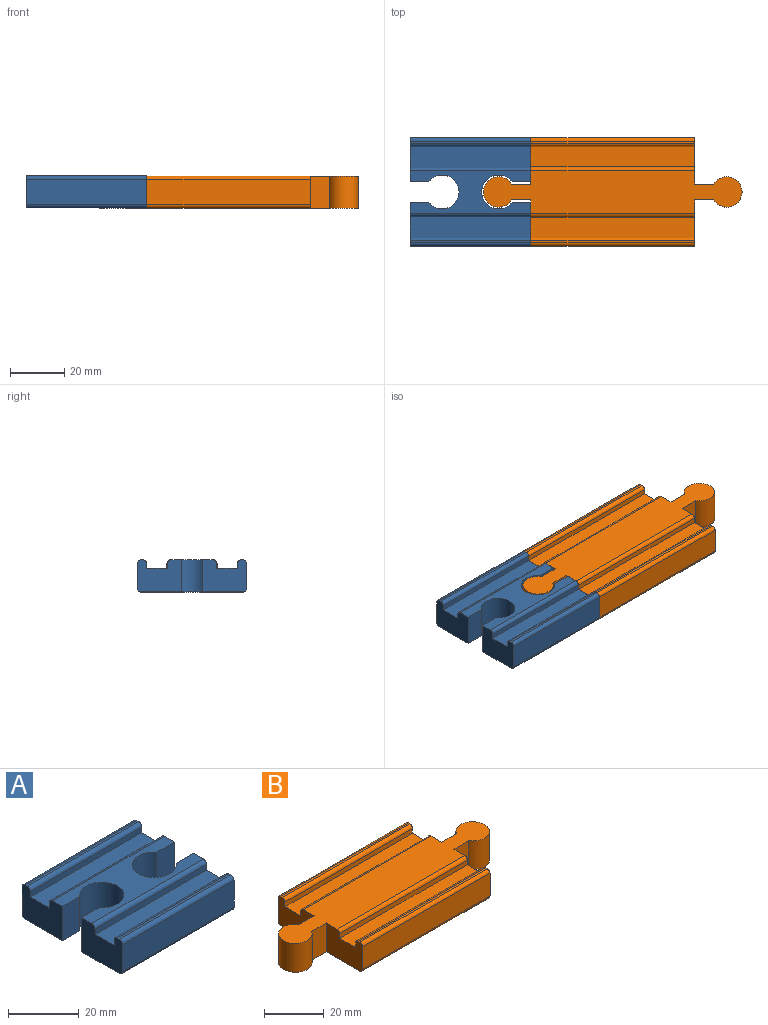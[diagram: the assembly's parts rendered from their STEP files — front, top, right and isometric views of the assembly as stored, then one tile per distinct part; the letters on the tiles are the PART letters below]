
ASSEMBLY  parts=2 mates=1
PART A: 30 faces, bbox 44.5x40x11.8 mm
  f0: plane 16.19x11.81mm, normal (-1,0,0), area 165.7mm2, adj f2,f3,f7,f9,f13,f14,f15,f18
  f1: plane 16.19x11.81mm, normal (1,0,0), area 165.7mm2, adj f2,f3,f7,f9,f13,f14,f15,f18
  f2: plane 44.45x15.62mm, normal (0,0,1), area 359.6mm2, adj f0,f1,f6,f8,f16,f18,f24,f25
  f3: plane 44.45x37.47mm, normal (0,0,-1), area 1330.5mm2, adj f0,f1,f6,f8,f20,f21,f24,f25
  f4: plane 44.45x0.76mm, normal (0,0,1), area 33.9mm2, adj f6,f8,f17,f23
  f5: plane 44.45x9.27mm, normal (0,1,0), area 412.1mm2, adj f6,f8,f21,f23
  f6: plane 16.19x11.81mm, normal (-1,0,0), area 165.7mm2, adj f2,f3,f4,f5,f10,f11,f12,f16
  f7: plane 44.45x9.27mm, normal (0,-1,0), area 412.1mm2, adj f0,f1,f20,f22
  f8: plane 16.19x11.81mm, normal (1,0,0), area 165.7mm2, adj f2,f3,f4,f5,f10,f11,f12,f16
  f9: plane 44.45x0.76mm, normal (0,0,1), area 33.9mm2, adj f0,f1,f19,f22
  f10: plane 44.45x1.91mm, normal (0,1,0), area 84.7mm2, adj f6,f8,f12,f16
  f11: plane 44.45x1.91mm, normal (0,-1,0), area 84.7mm2, adj f6,f8,f12,f17
  f12: plane 44.45x7.62mm, normal (0,0,1), area 338.7mm2, adj f6,f8,f10,f11
  f13: plane 44.45x1.91mm, normal (0,1,0), area 84.7mm2, adj f0,f1,f15,f19
  f14: plane 44.45x1.91mm, normal (0,-1,0), area 84.7mm2, adj f0,f1,f15,f18
  f15: plane 44.45x7.62mm, normal (0,0,1), area 338.7mm2, adj f0,f1,f13,f14
  f16: cylinder r=1.27mm len=44.45mm, axis (-1,0,0), area 88.7mm2, adj f2,f6,f8,f10
  f17: cylinder r=1.27mm len=44.45mm, axis (1,0,0), area 88.7mm2, adj f4,f6,f8,f11
  f18: cylinder r=1.27mm len=44.45mm, axis (1,0,0), area 88.7mm2, adj f0,f1,f2,f14
  f19: cylinder r=1.27mm len=44.45mm, axis (-1,0,0), area 88.7mm2, adj f0,f1,f9,f13
  f20: cylinder r=1.27mm len=44.45mm, axis (1,0,0), area 88.7mm2, adj f0,f1,f3,f7
  f21: cylinder r=1.27mm len=44.45mm, axis (-1,0,0), area 88.7mm2, adj f3,f5,f6,f8
  f22: cylinder r=1.27mm len=44.45mm, axis (-1,0,0), area 88.7mm2, adj f0,f1,f7,f9
  f23: cylinder r=1.27mm len=44.45mm, axis (1,0,0), area 88.7mm2, adj f4,f5,f6,f8
  f24: plane 11.81x6.89mm, normal (0,-1,0), area 81.4mm2, adj f2,f3,f8,f25
  f25: cylinder r=6.22mm len=12.45mm, axis (0,0,1), area 365mm2, adj f2,f3,f24,f26
  f26: plane 11.81x6.89mm, normal (0,1,0), area 81.4mm2, adj f1,f2,f3,f25
  f27: plane 11.81x6.89mm, normal (0,-1,0), area 81.4mm2, adj f2,f3,f6,f29
  f28: plane 11.81x6.89mm, normal (0,1,0), area 81.4mm2, adj f0,f2,f3,f29
  f29: cylinder r=6.22mm len=12.45mm, axis (0,0,1), area 365mm2, adj f2,f3,f27,f28
PART B: 30 faces, bbox 95.1x40x11.8 mm
  f0: plane 95.12x15.88mm, normal (0,0,1), area 1229.7mm2, adj f2,f3,f5,f7,f10,f11,f12,f13
  f1: plane 60.33x0.76mm, normal (0,0,1), area 46mm2, adj f5,f7,f23,f29
  f2: plane 17.08x11.81mm, normal (-1,0,0), area 176.6mm2, adj f0,f6,f8,f9,f15,f19,f20,f21
  f3: plane 17.08x11.81mm, normal (1,0,0), area 176.6mm2, adj f0,f6,f8,f9,f11,f19,f20,f21
  f4: plane 60.33x9.27mm, normal (0,1,0), area 559.3mm2, adj f5,f7,f27,f29
  f5: plane 17.08x11.81mm, normal (-1,0,0), area 176.6mm2, adj f0,f1,f4,f9,f13,f16,f17,f18
  f6: plane 60.33x9.27mm, normal (0,-1,0), area 559.3mm2, adj f2,f3,f26,f28
  f7: plane 17.08x11.81mm, normal (1,0,0), area 176.6mm2, adj f0,f1,f4,f9,f10,f16,f17,f18
  f8: plane 60.33x0.76mm, normal (0,0,1), area 46mm2, adj f2,f3,f24,f28
  f9: plane 95.12x37.47mm, normal (0,0,-1), area 2532.1mm2, adj f2,f3,f5,f7,f10,f11,f12,f13
  f10: plane 11.81x7.05mm, normal (0,1,0), area 83.2mm2, adj f0,f7,f9,f12
  f11: plane 11.81x7.05mm, normal (0,-1,0), area 83.2mm2, adj f0,f3,f9,f12
  f12: cylinder r=5.59mm len=11.81mm, axis (0,0,1), area 342.1mm2, adj f0,f9,f10,f11
  f13: plane 11.81x7.05mm, normal (0,1,0), area 83.2mm2, adj f0,f5,f9,f14
  f14: cylinder r=5.59mm len=11.81mm, axis (0,0,1), area 342.1mm2, adj f0,f9,f13,f15
  f15: plane 11.81x7.05mm, normal (0,-1,0), area 83.2mm2, adj f0,f2,f9,f14
  f16: plane 60.33x7.49mm, normal (0,0,1), area 452mm2, adj f5,f7,f17,f18
  f17: plane 60.33x1.91mm, normal (0,1,0), area 114.9mm2, adj f5,f7,f16,f22
  f18: plane 60.33x1.91mm, normal (0,-1,0), area 114.9mm2, adj f5,f7,f16,f23
  f19: plane 60.33x7.49mm, normal (0,0,1), area 452mm2, adj f2,f3,f20,f21
  f20: plane 60.33x1.91mm, normal (0,1,0), area 114.9mm2, adj f2,f3,f19,f24
  f21: plane 60.33x1.91mm, normal (0,-1,0), area 114.9mm2, adj f2,f3,f19,f25
  f22: cylinder r=1.27mm len=60.33mm, axis (-1,0,0), area 120.3mm2, adj f0,f5,f7,f17
  f23: cylinder r=1.27mm len=60.33mm, axis (1,0,0), area 120.3mm2, adj f1,f5,f7,f18
  f24: cylinder r=1.27mm len=60.33mm, axis (-1,0,0), area 120.3mm2, adj f2,f3,f8,f20
  f25: cylinder r=1.27mm len=60.33mm, axis (1,0,0), area 120.3mm2, adj f0,f2,f3,f21
  f26: cylinder r=1.27mm len=60.33mm, axis (1,0,0), area 120.3mm2, adj f2,f3,f6,f9
  f27: cylinder r=1.27mm len=60.33mm, axis (-1,0,0), area 120.3mm2, adj f4,f5,f7,f9
  f28: cylinder r=1.27mm len=60.33mm, axis (-1,0,0), area 120.3mm2, adj f2,f3,f6,f8
  f29: cylinder r=1.27mm len=60.33mm, axis (1,0,0), area 120.3mm2, adj f1,f4,f5,f7
PLACE A t=(5.68,22.21,-32.68)mm
PLACE B t=(58.07,22.21,-32.74)mm
MATE slider A.f25 <-> B.f14  axis (0,0,1) through (16.09,22.21,-20.87)mm
